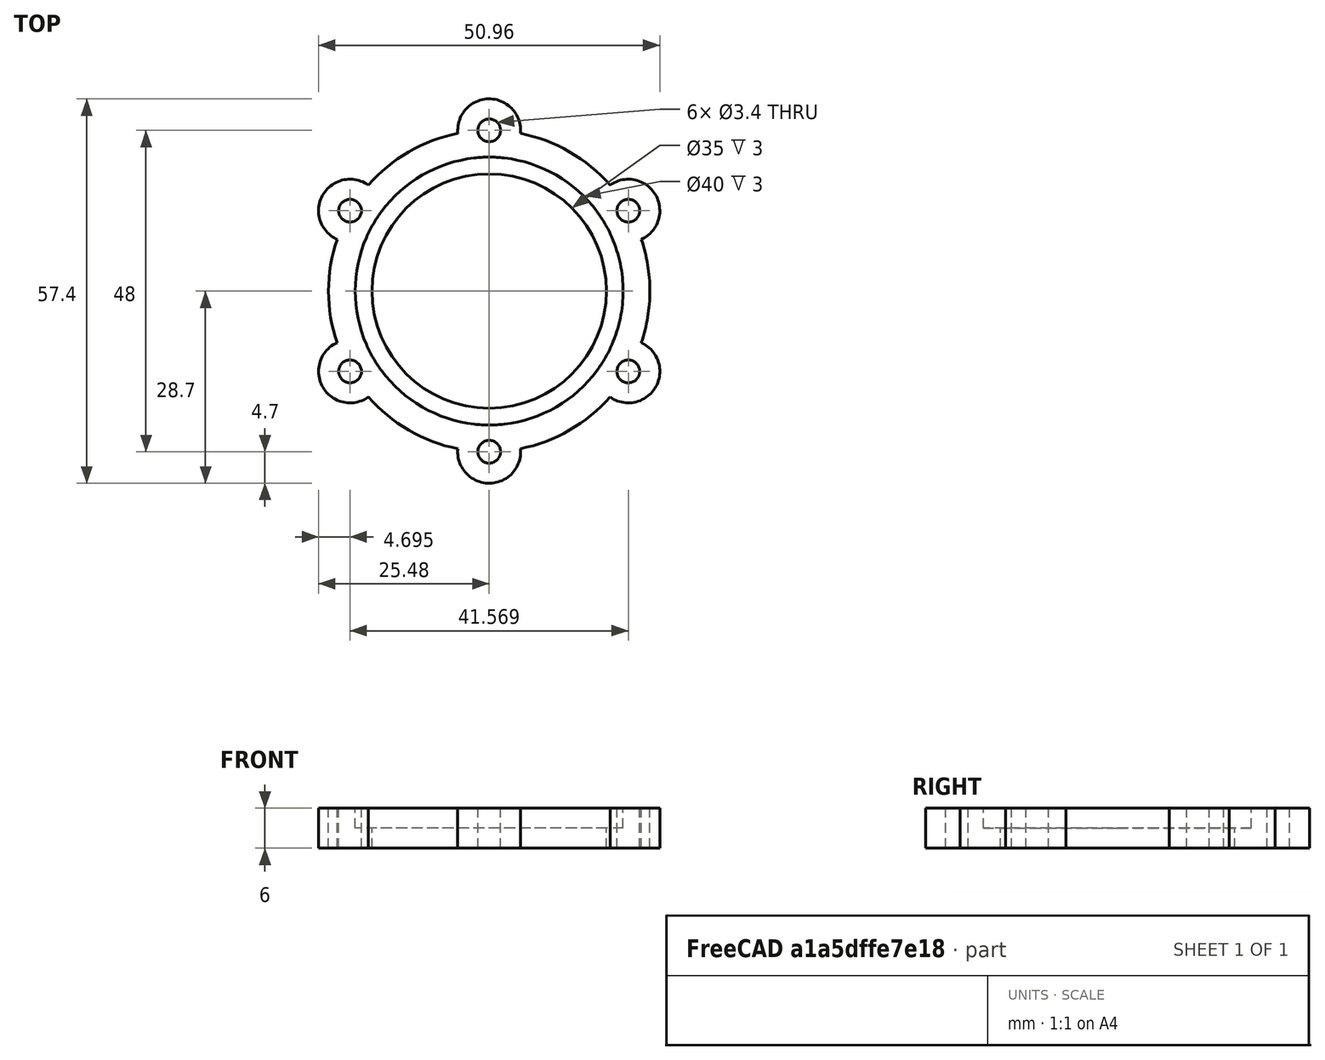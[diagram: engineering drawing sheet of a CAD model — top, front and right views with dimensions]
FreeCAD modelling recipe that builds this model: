
FCSTD DOCUMENT  (FreeCAD 0.18R16033 (Git))
Label: ceramic_holddown_clamp
License: All rights reserved
LicenseURL: http://en.wikipedia.org/wiki/All_rights_reserved
objects: Part::Cylinder×5, Part::FeaturePython×2, Part::MultiFuse×2, Part::Cut×1
note: 10 computed .brp shape members not serialized (recipe doc carries the construction recipe); baked Part::Feature solids carry a one-line shape summary decoded from their .brp

FEATURE [Part::Cylinder] Cylinder
  Angle = 360
  AttacherType = Attacher::AttachEngine3D
  Height = 3
  Placement = pos=(0,0,3) rot=(0,0,1;0rad)
  Radius = 20
FEATURE [Part::Cylinder] Cylinder001
  Angle = 360
  AttacherType = Attacher::AttachEngine3D
  Height = 6
  Radius = 24
FEATURE [Part::Cylinder] Cylinder002
  Angle = 360
  AttacherType = Attacher::AttachEngine3D
  Height = 10
  Radius = 17.5
FEATURE [Part::Cylinder] Cylinder003
  Angle = 360
  AttacherType = Attacher::AttachEngine3D
  Height = 10
  Placement = pos=(0,-24,0) rot=(0,0,1;0rad)
  Radius = 1.7
FEATURE [Part::Cylinder] Cylinder004
  Angle = 360
  AttacherType = Attacher::AttachEngine3D
  Height = 6
  Placement = pos=(0,-24,0) rot=(0,0,1;0rad)
  Radius = 4.7
FEATURE [Part::FeaturePython] Array  # Draft array (typed FeaturePython)
  Angle = 360
  ArrayType = 1
  Axis = (0,0,1)
  Base = -> Cylinder004
  Center = (0,0,0)
  Fuse = false
  IntervalAxis = (0,0,0)
  IntervalX = (1,0,0)
  IntervalY = (0,1,0)
  IntervalZ = (0,0,1)
  NumberPolar = 6
  NumberX = 2
  NumberY = 2
  NumberZ = 1
FEATURE [Part::FeaturePython] Array001  # Draft array (typed FeaturePython)
  Angle = 360
  ArrayType = 1
  Axis = (0,0,1)
  Base = -> Cylinder003
  Center = (0,0,0)
  Fuse = false
  IntervalAxis = (0,0,0)
  IntervalX = (1,0,0)
  IntervalY = (0,1,0)
  IntervalZ = (0,0,1)
  NumberPolar = 6
  NumberX = 2
  NumberY = 2
  NumberZ = 1
FEATURE [Part::MultiFuse] Fusion
  Shapes = -> [Array,Cylinder001]
FEATURE [Part::MultiFuse] Fusion001
  Shapes = -> [Array001,Cylinder002,Cylinder]
FEATURE [Part::Cut] Cut
  Base = -> Fusion
  Tool = -> Fusion001
